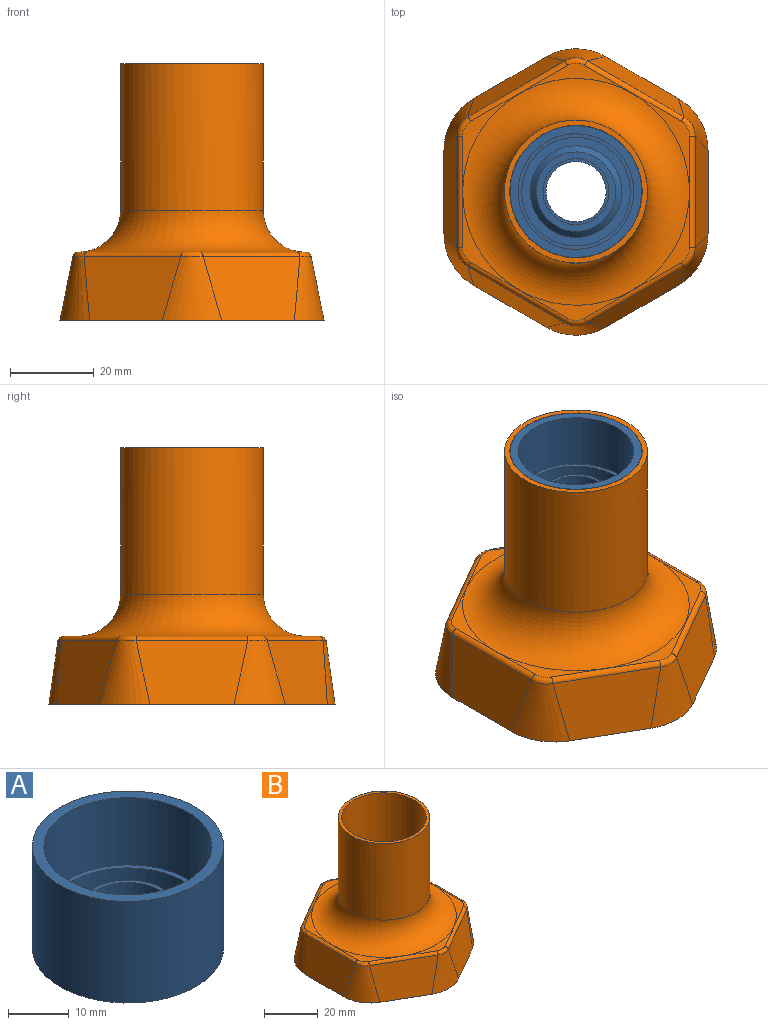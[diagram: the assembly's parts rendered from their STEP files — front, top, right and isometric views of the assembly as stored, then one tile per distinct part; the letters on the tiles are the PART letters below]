
ASSEMBLY  parts=2 mates=1
PART A: 14 faces, bbox 31.4x31.4x20.4 mm
  f0: cylinder r=12.95mm len=25.9mm, axis (0,0,-1), area 447.5mm2, adj f1,f13
  f1: plane 25.9x25.9mm, normal (0,0,1), area 151.9mm2, adj f0,f2
  f2: cylinder r=10.93mm len=21.85mm, axis (0,0,-1), area 223.1mm2, adj f1,f3
  f3: cone r=9.48mm half-angle=44deg, axis (0,0,-1), area 133.7mm2, adj f2,f4
  f4: plane 18.95x18.95mm, normal (0,0,1), area 87.2mm2, adj f3,f5
  f5: cylinder r=7.88mm len=15.75mm, axis (0,0,-1), area 94mm2, adj f4,f6
  f6: plane 15.75x15.75mm, normal (0,0,1), area 33.1mm2, adj f5,f7
  f7: cylinder r=7.17mm len=14.35mm, axis (0,0,-1), area 135.2mm2, adj f6,f8
  f8: cone r=7.17mm half-angle=35deg, axis (0,0,-1), area 346.4mm2, adj f7,f9
  f9: plane 31.4x31.4mm, normal (0,0,-1), area 413.9mm2, adj f8,f10
  f10: cylinder r=15.7mm len=31.4mm, axis (0,0,-1), area 2012.4mm2, adj f9,f11
  f11: plane 31.4x31.4mm, normal (0,0,1), area 176.1mm2, adj f10,f12
  f12: cylinder r=13.8mm len=27.6mm, axis (0,0,-1), area 1170.6mm2, adj f11,f13
  f13: plane 27.6x27.6mm, normal (0,0,1), area 71.4mm2, adj f0,f12
PART B: 68 faces, bbox 63.4x72.7x62.2 mm
  f0: cone r=26.7mm half-angle=3.4deg, axis (0,0,-1), area 400.7mm2, adj f9,f21,f22,f31
  f1: bspline ~11.26x2.07mm, area 16.4mm2, adj f7,f8,f10,f22
  f2: plane 5.98x2.65mm, normal (0,0,1), area 9.1mm2, adj f3,f4,f31,f66
  f3: cylinder r=25.55mm len=13.22mm, axis (0,0,1), area 15.9mm2, adj f2,f4,f5,f6,f66
  f4: plane 1.53x1.25mm, normal (-0.96,-0.29,0), area 2mm2, adj f2,f3,f5,f31
  f5: plane 14.05x2.72mm, normal (0,0,-1), area 22.1mm2, adj f3,f4,f6,f31
  f6: plane 1.56x1.05mm, normal (0.97,-0.22,0), area 1.7mm2, adj f3,f5,f31,f66
  f7: cone r=25.1mm half-angle=2.6deg, axis (0,0,-1), area 31.9mm2, adj f1,f8,f9,f22
  f8: plane 3.66x3.05mm, normal (0,0,-1), area 5.6mm2, adj f1,f7,f9,f10,f31
  f9: plane 10.1x1.78mm, normal (-0.87,-0.5,0), area 16.7mm2, adj f0,f7,f8,f22,f31
  f10: plane 10.1x0.44mm, normal (0.93,0.37,0), area 0.8mm2, adj f1,f8,f22,f31,f32
  f11: cone r=26.7mm half-angle=3.4deg, axis (0,0,-1), area 400.7mm2, adj f20,f22,f31,f35
  f12: bspline ~11.26x1.58mm, area 16.4mm2, adj f18,f19,f21,f22
  f13: plane 5.11x5.05mm, normal (0,0,1), area 9.1mm2, adj f14,f15,f31,f67
  f14: cylinder r=25.55mm len=11.22mm, axis (0,0,1), area 15.9mm2, adj f13,f15,f16,f17,f67
  f15: plane 1.25x1.17mm, normal (0.73,-0.68,0), area 2mm2, adj f13,f14,f16,f31
  f16: plane 12.39x8.54mm, normal (0,0,-1), area 22.1mm2, adj f14,f15,f17,f31
  f17: plane 1.53x1.05mm, normal (-0.29,0.96,0), area 1.7mm2, adj f14,f16,f31,f67
  f18: cone r=25.1mm half-angle=2.6deg, axis (0,0,-1), area 31.9mm2, adj f12,f19,f20,f22
  f19: plane 3.94x3.15mm, normal (0,0,-1), area 5.6mm2, adj f12,f18,f20,f21,f31
  f20: plane 10.1x1.78mm, normal (0.87,-0.5,0), area 16.7mm2, adj f11,f18,f19,f22,f31
  f21: plane 10.1x0.37mm, normal (-0.79,0.62,0), area 0.8mm2, adj f0,f12,f19,f22,f31
  f22: plane 53.4x53.4mm, normal (0,0,-1), area 1438.9mm2, adj f0,f1,f7,f9,f10,f11,f12,f18
  f23: plane 23.09x15.26mm, normal (0.49,-0.85,0.2), area 363.4mm2, adj f29,f46,f51,f61
  f24: plane 26.66x15.26mm, normal (0.98,0,0.2), area 363.4mm2, adj f29,f50,f51,f57
  f25: plane 23.09x15.26mm, normal (0.49,0.85,0.2), area 363.4mm2, adj f29,f49,f50,f53
  f26: plane 23.09x15.26mm, normal (-0.49,0.85,0.2), area 363.4mm2, adj f29,f48,f49,f56
  f27: plane 26.66x15.26mm, normal (-0.98,0,0.2), area 363.4mm2, adj f29,f47,f48,f60
  f28: plane 23.09x15.26mm, normal (-0.49,-0.85,0.2), area 363.4mm2, adj f29,f46,f47,f64
  f29: plane 68.31x63mm, normal (0,0,-1), area 1055.4mm2, adj f23,f24,f25,f26,f27,f28,f31,f46
  f30: plane 61.39x54.27mm, normal (0,0,1), area 246.8mm2, adj f52,f53,f54,f55,f56,f57,f58,f59
  f31: cylinder r=27.15mm len=54.3mm, axis (0,0,1), area 944.2mm2, adj f0,f2,f4,f5,f6,f8,f9,f10
  f32: cone r=26.7mm half-angle=3.4deg, axis (0,0,-1), area 400.7mm2, adj f10,f22,f31,f36
  f33: cone r=25.1mm half-angle=2.6deg, axis (0,0,-1), area 31.9mm2, adj f22,f34,f36,f42
  f34: plane 3.78x1.8mm, normal (0,0,-1), area 5.6mm2, adj f31,f33,f35,f36,f42
  f35: plane 10.1x0.47mm, normal (-0.14,-0.99,0), area 0.8mm2, adj f11,f22,f31,f34,f42
  f36: plane 10.1x2.05mm, normal (0,1,0), area 16.7mm2, adj f22,f31,f32,f33,f34
  f37: plane 6.1x3.25mm, normal (0,0,1), area 9.1mm2, adj f31,f38,f41,f65
  f38: cylinder r=25.55mm len=11.68mm, axis (0,0,1), area 15.9mm2, adj f37,f39,f40,f41,f65
  f39: plane 12.77x7.77mm, normal (0,0,-1), area 22.1mm2, adj f31,f38,f40,f41
  f40: plane 1.17x1.09mm, normal (-0.68,-0.73,0), area 1.7mm2, adj f31,f38,f39,f65
  f41: plane 1.56x1.25mm, normal (0.22,0.97,0), area 2mm2, adj f31,f37,f38,f39
  f42: bspline ~10.24x1.96mm, area 16.4mm2, adj f22,f33,f34,f35
  f43: cylinder r=15.8mm len=47.7mm, axis (0,0,-1), area 4735.4mm2, adj f22,f45
  f44: cylinder r=17.05mm len=35mm, axis (0,0,-1), area 3749.5mm2, adj f45,f52
  f45: plane 34.1x34.1mm, normal (0,0,1), area 129mm2, adj f43,f44
  f46: bspline ~17.24x14.7mm, area 157.2mm2, adj f23,f28,f29,f63
  f47: bspline ~17.24x12.73mm, area 157.2mm2, adj f27,f28,f29,f62
  f48: bspline ~17.24x12.73mm, area 157.2mm2, adj f26,f27,f29,f58
  f49: bspline ~17.24x14.7mm, area 157.2mm2, adj f25,f26,f29,f54
  f50: bspline ~17.24x12.73mm, area 157.2mm2, adj f24,f25,f29,f55
  f51: bspline ~17.24x12.73mm, area 157.2mm2, adj f23,f24,f29,f59
  f52: torus R=27.05mm, axis (0,0,-1), area 2041.4mm2, adj f30,f44
  f53: cylinder r=1.3mm len=23.73mm, axis (-0.87,0.5,0), area 47.5mm2, adj f25,f30,f54,f55
  f54: bspline ~5.49x1.87mm, area 9.2mm2, adj f30,f49,f53,f56
  f55: bspline ~4.76x3.38mm, area 9.2mm2, adj f30,f50,f53,f57
  f56: cylinder r=1.3mm len=23.73mm, axis (-0.87,-0.5,0), area 47.5mm2, adj f26,f30,f54,f58
  f57: cylinder r=1.3mm len=26.66mm, axis (0,1,0), area 47.5mm2, adj f24,f30,f55,f59
  f58: bspline ~4.76x3.38mm, area 9.2mm2, adj f30,f48,f56,f60
  f59: bspline ~4.76x3.38mm, area 9.2mm2, adj f30,f51,f57,f61
  f60: cylinder r=1.3mm len=26.66mm, axis (0,-1,0), area 47.5mm2, adj f27,f30,f58,f62
  f61: cylinder r=1.3mm len=23.73mm, axis (0.87,0.5,0), area 47.5mm2, adj f23,f30,f59,f63
  f62: bspline ~4.76x3.38mm, area 9.2mm2, adj f30,f47,f60,f64
  f63: bspline ~5.49x1.87mm, area 9.2mm2, adj f30,f46,f61,f64
  f64: cylinder r=1.3mm len=23.73mm, axis (0.87,-0.5,0), area 47.5mm2, adj f28,f30,f62,f63
  f65: plane 7.82x5.75mm, normal (-0.02,-0.02,1), area 13mm2, adj f31,f37,f38,f40
  f66: plane 8.45x2.26mm, normal (0.02,-0.01,1), area 13mm2, adj f2,f3,f6,f31
  f67: plane 7.77x5.1mm, normal (-0.01,0.02,1), area 13mm2, adj f13,f14,f17,f31
PLACE A t=(60.35,-0.13,7.6)mm
PLACE B t=(-0.35,-0.13,-33.3)mm
MATE revolute A.f8 <-> B.f43  axis (0,0,-1) through (-0.35,-0.13,28)mm
